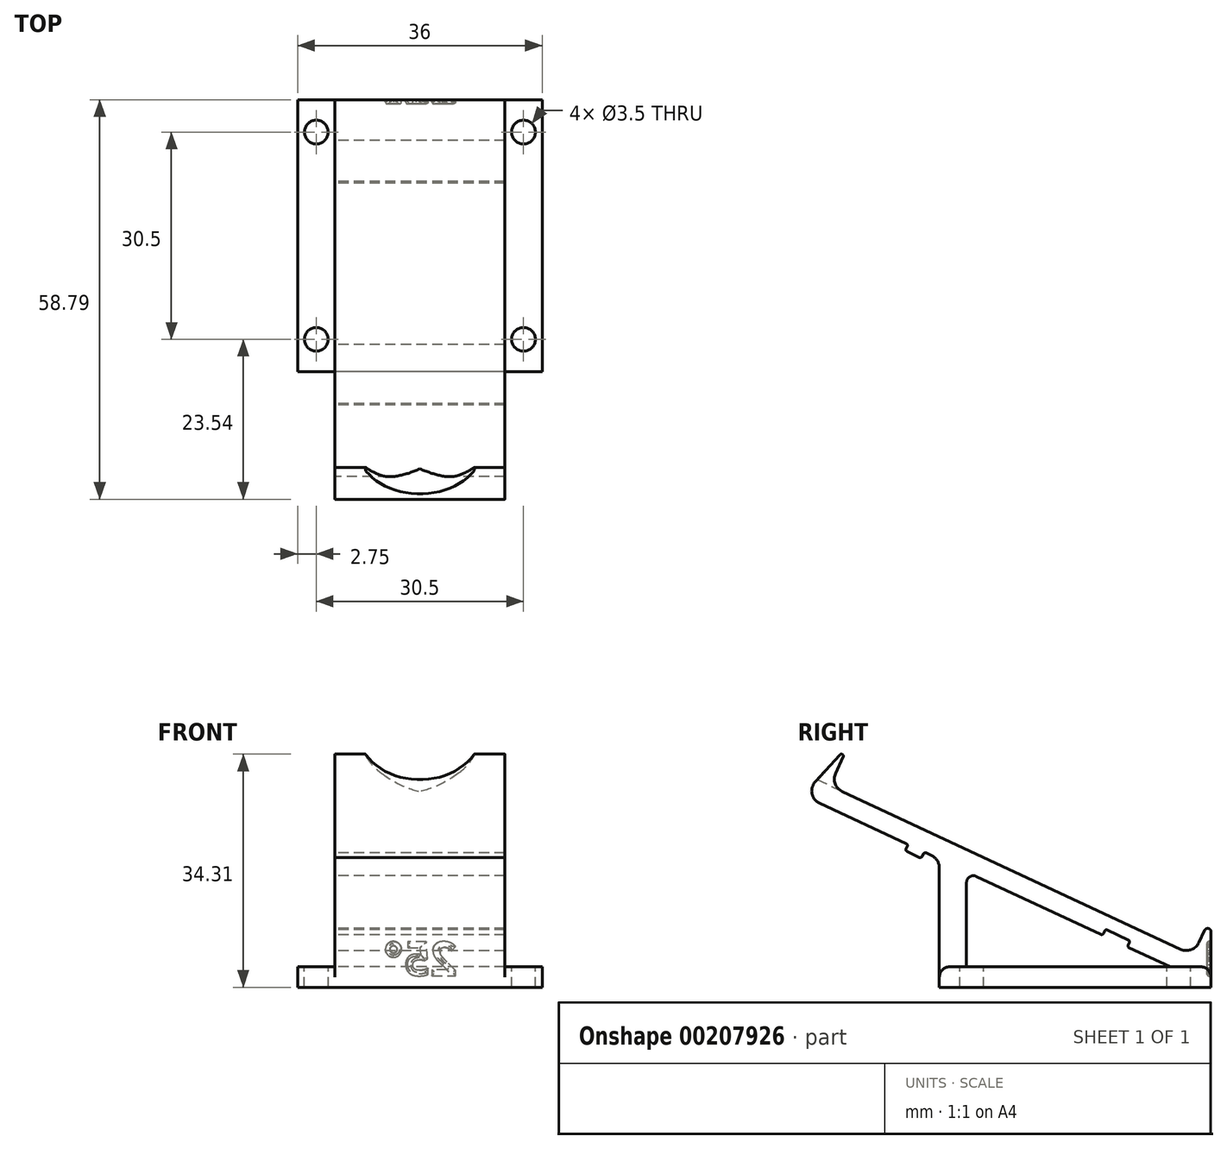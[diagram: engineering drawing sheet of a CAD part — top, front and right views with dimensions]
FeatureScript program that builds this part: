
annotation { "Feature Type Name" : "Feature", "Feature Type Description" : "" }
export const myFeature = defineFeature(function(context is Context, id is Id, definition is map)
    precondition{}
    {
        {
            var Q0;
            Q0=qCreatedBy(makeId("Right.planeOp"),FACE);
            var sketch = newSketch(context, id + "F0", { "sketchPlane" : qUnion([Q0])});
            skLineSegment(sketch, "E0", {"start": v(0, 0) * mm, "end": v(4, 0) * mm});
            skLineSegment(sketch, "E1", {"start": v(24.16, 4.92) * mm, "end": v(24.33, 5.28) * mm});
            skLineSegment(sketch, "E2", {"start": v(24.73, 5.43) * mm, "end": v(27.8, 4) * mm});
            skLineSegment(sketch, "E3", {"start": v(27.95, 3.6) * mm, "end": v(27.78, 3.23) * mm});
            skLineSegment(sketch, "E4", {"start": v(27.93, 2.83) * mm, "end": v(34, 0) * mm});
            skLineSegment(sketch, "E5", {"start": v(40, 0) * mm, "end": v(40, 5.16) * mm});
            skLineSegment(sketch, "E6", {"start": v(39.05, 5.37) * mm, "end": v(38.2, 3.56) * mm});
            skLineSegment(sketch, "E7", {"start": v(35.54, 2.6) * mm, "end": v(-14.3, 25.83) * mm});
            skLineSegment(sketch, "E8", {"start": v(-15.27, 28.5) * mm, "end": v(-14.16, 30.88) * mm});
            skLineSegment(sketch, "E9", {"start": v(-14.65, 31.2) * mm, "end": v(-18.27, 27.24) * mm});
            skLineSegment(sketch, "E10", {"start": v(-17.64, 24.08) * mm, "end": v(-4.86, 18.12) * mm});
            skLineSegment(sketch, "E11", {"start": v(-4.71, 17.72) * mm, "end": v(-4.88, 17.36) * mm});
            skLineSegment(sketch, "E12", {"start": v(-4.74, 16.96) * mm, "end": v(-2.93, 16.12) * mm});
            skLineSegment(sketch, "E13", {"start": v(-2.53, 16.26) * mm, "end": v(-2.36, 16.62) * mm});
            skLineSegment(sketch, "E14", {"start": v(-1.96, 16.77) * mm, "end": v(-1.15, 16.4) * mm});
            skLineSegment(sketch, "E15", {"start": v(0, 14.58) * mm, "end": v(0, 0) * mm});
            skArc(sketch, "E16", {"start": v(23.76, 4.78) * mm, "mid": v(23.99, 4.77) * mm, "end": v(24.16, 4.92) * mm});
            skArc(sketch, "E17", {"start": v(24.33, 5.28) * mm, "mid": v(24.5, 5.44) * mm, "end": v(24.73, 5.43) * mm});
            skArc(sketch, "E18", {"start": v(27.8, 4) * mm, "mid": v(27.96, 3.82) * mm, "end": v(27.95, 3.6) * mm});
            skArc(sketch, "E19", {"start": v(27.78, 3.23) * mm, "mid": v(27.77, 3) * mm, "end": v(27.93, 2.83) * mm});
            skArc(sketch, "E20", {"start": v(35.54, 2.6) * mm, "mid": v(37.07, 2.52) * mm, "end": v(38.2, 3.56) * mm});
            skArc(sketch, "E21", {"start": v(40, 5.16) * mm, "mid": v(39.6, 5.65) * mm, "end": v(39.05, 5.37) * mm});
            skArc(sketch, "E22", {"start": v(-1.15, 16.4) * mm, "mid": v(-0.31, 15.65) * mm, "end": v(0, 14.58) * mm});
            skArc(sketch, "E23", {"start": v(-1.96, 16.77) * mm, "mid": v(-2.19, 16.78) * mm, "end": v(-2.36, 16.62) * mm});
            skArc(sketch, "E24", {"start": v(-2.93, 16.12) * mm, "mid": v(-2.7, 16.1) * mm, "end": v(-2.53, 16.26) * mm});
            skArc(sketch, "E25", {"start": v(-4.74, 16.96) * mm, "mid": v(-4.9, 17.13) * mm, "end": v(-4.88, 17.36) * mm});
            skArc(sketch, "E26", {"start": v(-4.86, 18.12) * mm, "mid": v(-4.7, 17.95) * mm, "end": v(-4.71, 17.72) * mm});
            skArc(sketch, "E27", {"start": v(-17.64, 24.08) * mm, "mid": v(-18.75, 25.5) * mm, "end": v(-18.27, 27.24) * mm});
            skArc(sketch, "E28", {"start": v(-14.65, 31.2) * mm, "mid": v(-14.26, 31.26) * mm, "end": v(-14.16, 30.88) * mm});
            skPoint(sketch, "E29.visualSharp", {"position": v(-16.12, 26.68) * mm});
            skArc(sketch, "E30.filletArc", {"start": v(-15.27, 28.5) * mm, "mid": v(-15.34, 26.96) * mm, "end": v(-14.3, 25.83) * mm});
            skLineSegment(sketch, "E31", {"start": v(34, 0) * mm, "end": v(40, 0) * mm});
            skLineSegment(sketch, "E32", {"start": v(4, 12.42) * mm, "end": v(4, 0) * mm});
            skLineSegment(sketch, "E33", {"start": v(5.42, 13.33) * mm, "end": v(23.76, 4.78) * mm});
            skPoint(sketch, "E34.visualSharp", {"position": v(4, 13.99) * mm});
            skArc(sketch, "E34.filletArc", {"start": v(5.42, 13.33) * mm, "mid": v(4.46, 13.26) * mm, "end": v(4, 12.42) * mm});
            skSolve(sketch);
        }
        {
            var Q0;
            Q0 = qSketchRegion(id + "F0", true);
            extrude(context, id + "F1", {"entities" : qUnion([Q0]), "endBound" : BoundingType.SYMMETRIC, "depth" : 25 * mm});
        }
        {
            var Q0;
            Q0=makeQuery(id+"F1.opExtrude","SWEPT_FACE",FACE,{"disambiguationData":[OSD([sQuery(id+"F0.wireOp",EDGE,"E0")])]});
            var sketch = newSketch(context, id + "F2", { "sketchPlane" : qUnion([Q0])});
            skLineSegment(sketch, "E35.bottom", {"start": v(15.25, -4.75) * mm, "end": v(-15.25, -4.75) * mm, "construction": true});
            skLineSegment(sketch, "E35.top", {"start": v(15.25, -35.25) * mm, "end": v(-15.25, -35.25) * mm, "construction": true});
            skLineSegment(sketch, "E35.left", {"start": v(15.25, -4.75) * mm, "end": v(15.25, -35.25) * mm, "construction": true});
            skLineSegment(sketch, "E35.right", {"start": v(-15.25, -4.75) * mm, "end": v(-15.25, -35.25) * mm, "construction": true});
            skCircle(sketch, "E36", {"center": v(-15.25, -4.75) * mm, "radius": 1.75 * mm});
            skCircle(sketch, "E37", {"center": v(15.25, -4.75) * mm, "radius": 1.75 * mm});
            skCircle(sketch, "E38", {"center": v(15.25, -35.25) * mm, "radius": 1.75 * mm});
            skCircle(sketch, "E39", {"center": v(-15.25, -35.25) * mm, "radius": 1.75 * mm});
            skLineSegment(sketch, "E40", {"start": v(-15.25, -4.75) * mm, "end": v(-15.25, 0) * mm, "construction": true});
            skLineSegment(sketch, "E41", {"start": v(-15.25, -35.25) * mm, "end": v(-15.25, -40) * mm, "construction": true});
            skLineSegment(sketch, "E42.bottom", {"start": v(-18, 0) * mm, "end": v(18, 0) * mm});
            skLineSegment(sketch, "E42.top", {"start": v(-18, -40) * mm, "end": v(18, -40) * mm});
            skLineSegment(sketch, "E42.left", {"start": v(-18, 0) * mm, "end": v(-18, -40) * mm});
            skLineSegment(sketch, "E42.right", {"start": v(18, 0) * mm, "end": v(18, -40) * mm});
            skLineSegment(sketch, "E43", {"start": v(15.25, -4.75) * mm, "end": v(18, -4.75) * mm, "construction": true});
            skLineSegment(sketch, "E44", {"start": v(-15.25, -4.75) * mm, "end": v(-18, -4.75) * mm, "construction": true});
            skPoint(sketch, "E45.endSnap0", {"position": v(0, 0) * mm});
            skLineSegment(sketch, "E46", {"start": v(0, 0) * mm, "end": v(0, -40) * mm, "construction": true});
            skLineSegment(sketch, "E47", {"start": v(-12.42, -20) * mm, "end": v(12.9, -20) * mm, "construction": true});
            skPoint(sketch, "E47.startSnap0", {"position": v(0, -20) * mm});
            skSolve(sketch);
        }
        {
            var Q0;
            Q0 = qSketchRegion(id + "F2", true);
            extrude(context, id + "F3", {"entities" : qUnion([Q0]), "operationType" : NewBodyOperationType.ADD, "depth" : 3 * mm});
        }
        {
            var Q0;
            Q0=makeQuery(id+"F1.opExtrude","SWEPT_FACE",FACE,{"disambiguationData":[OSD([sQuery(id+"F0.wireOp",EDGE,"E8")])]});
            var sketch = newSketch(context, id + "F4", { "sketchPlane" : qUnion([Q0])});
            skCircle(sketch, "E48", {"center": v(0, 26.37) * mm, "radius": 9 * mm});
            skLineSegment(sketch, "E49.0", {"start": v(-12.5, 17.37) * mm, "end": v(12.5, 17.37) * mm, "construction": true});
            skLineSegment(sketch, "E50", {"start": v(0, 17.37) * mm, "end": v(0, 34.14) * mm, "construction": true});
            skSolve(sketch);
        }
        {
            var Q0;
            Q0 = qSketchRegion(id + "F4", true);
            var Q1;
            Q1=makeQuery(id+"F1.opExtrude","SWEPT_FACE",FACE,{"disambiguationData":[OSD([sQuery(id+"F0.wireOp",EDGE,"E9")])]});
            var Q2;
            Q2=makeQuery(id+"F1.opExtrude","SWEPT_FACE",FACE,{"disambiguationData":[OSD([sQuery(id+"F0.wireOp",EDGE,"E7")])]});
            extrude(context, id + "F5", {"entities" : qUnion([Q0]), "operationType" : NewBodyOperationType.REMOVE, "endBound" : BoundingType.UP_TO_SURFACE, "oppositeDirection" : true, "endBoundEntityFace" : qUnion([Q1]), "depth" : 25 * mm, "hasSecondDirection" : true, "secondDirectionOppositeDirection" : false, "secondDirectionBoundEntityFace" : qUnion([Q2]), "secondDirectionDepth" : 2 * mm});
        }
        {
            var Q0;
            {var subQ0=sQuery(id+"F2.wireOp",EDGE,"E42.bottom");var subQ1=sQuery(id+"F2.wireOp",EDGE,"E42.right");Q0=makeQuery(id+"F3.boolean.opBoolean","SPLIT",EDGE,{"disambiguationData":[TD([makeQuery(id+"F3.opExtrude","SWEPT_FACE",FACE,{"disambiguationData":[OSD([subQ1])]})])],"derivedFrom":makeQuery(id+"F3.opExtrude","CAP_EDGE",EDGE,{"disambiguationData":[OSD([subQ0])],"isStart":true})});}
            var Q1;
            {var subQ0=sQuery(id+"F2.wireOp",EDGE,"E42.top");var subQ1=sQuery(id+"F2.wireOp",EDGE,"E42.right");Q1=makeQuery(id+"F3.boolean.opBoolean","SPLIT",EDGE,{"disambiguationData":[TD([makeQuery(id+"F3.opExtrude","SWEPT_FACE",FACE,{"disambiguationData":[OSD([subQ1])]})])],"derivedFrom":makeQuery(id+"F3.opExtrude","CAP_EDGE",EDGE,{"disambiguationData":[OSD([subQ0])],"isStart":true})});}
            var Q2;
            {var subQ0=sQuery(id+"F2.wireOp",EDGE,"E42.top");var subQ1=sQuery(id+"F2.wireOp",EDGE,"E42.left");Q2=makeQuery(id+"F3.boolean.opBoolean","SPLIT",EDGE,{"disambiguationData":[TD([makeQuery(id+"F3.opExtrude","SWEPT_FACE",FACE,{"disambiguationData":[OSD([subQ1])]})])],"derivedFrom":makeQuery(id+"F3.opExtrude","CAP_EDGE",EDGE,{"disambiguationData":[OSD([subQ0])],"isStart":true})});}
            var Q3;
            {var subQ0=sQuery(id+"F2.wireOp",EDGE,"E42.bottom");var subQ2=sQuery(id+"F2.wireOp",EDGE,"E42.left");Q3=makeQuery(id+"F3.boolean.opBoolean","SPLIT",EDGE,{"disambiguationData":[TD([makeQuery(id+"F3.opExtrude","SWEPT_FACE",FACE,{"disambiguationData":[OSD([subQ2])]})])],"derivedFrom":makeQuery(id+"F3.opExtrude","CAP_EDGE",EDGE,{"disambiguationData":[OSD([subQ0])],"isStart":true})});}
            var Q4;
            Q4=makeQuery(id+"F1.opExtrude","SWEPT_EDGE",EDGE,{"disambiguationData":[OSD([sQuery(id+"F0.wireOp",EDGE,"E0"),sQuery(id+"F0.wireOp",EDGE,"E32")])]});
            fillet(context, id + "F6", {"entities" : qUnion([Q0, Q1, Q2, Q3, Q4]), "radius" : 1.5 * mm, "tangentPropagation" : true, "allowEdgeOverflow" : false});
        }
        {
            var Q0;
            Q0=makeQuery(id+"F3.boolean.opBoolean","MERGE",FACE,{"derivedFrom":[makeQuery(id+"F1.opExtrude","SWEPT_FACE",FACE,{"disambiguationData":[OSD([sQuery(id+"F0.wireOp",EDGE,"E5")])]}),makeQuery(id+"F3.opExtrude","SWEPT_FACE",FACE,{"disambiguationData":[OSD([sQuery(id+"F2.wireOp",EDGE,"a0c96e45-3273-4dbd-95e5-2c47b5aee7d6.top")])]})]});
            var sketch = newSketch(context, id + "F7", { "sketchPlane" : qUnion([Q0])});
            skText(sketch, "E51", { "text": "25°", "fontName": "OpenSans-Bold.ttf"});
            skPoint(sketch, "E52.startSnap0", {"position": v(0, 1.08) * mm});
            skPoint(sketch, "E52.endSnap0", {"position": v(0, 1.08) * mm});
            skLineSegment(sketch, "E53.0", {"start": v(12.5, -1.5) * mm, "end": v(12.5, 5.16) * mm, "construction": true});
            skLineSegment(sketch, "E54.0", {"start": v(-12.5, 5.16) * mm, "end": v(12.5, 5.16) * mm, "construction": true});
            skLineSegment(sketch, "E55.0", {"start": v(-12.5, -1.5) * mm, "end": v(-12.5, 5.16) * mm, "construction": true});
            skLineSegment(sketch, "E56", {"start": v(5.52, 3.58) * mm, "end": v(5.52, 5.16) * mm, "construction": true});
            skLineSegment(sketch, "E57", {"start": v(5.52, -1.42) * mm, "end": v(5.52, -3) * mm, "construction": true});
            skLineSegment(sketch, "E58.0", {"start": v(18, -3) * mm, "end": v(-18, -3) * mm, "construction": true});
            skLineSegment(sketch, "E59", {"start": v(-5.52, 3.58) * mm, "end": v(-12.5, 3.58) * mm, "construction": true});
            skLineSegment(sketch, "E60", {"start": v(5.52, 3.58) * mm, "end": v(12.5, 3.58) * mm, "construction": true});
            const initialGuessF7  = {"E51": [-0.00552, -0.00128, 1, 0, 0.005]};
            skSetInitialGuess(sketch, initialGuessF7);
            skSolve(sketch);
        }
        {
            var Q0;
            Q0 = qSketchRegion(id + "F7", true);
            extrude(context, id + "F8", {"entities" : qUnion([Q0]), "operationType" : NewBodyOperationType.REMOVE, "oppositeDirection" : true, "depth" : .6 * mm});
        }
        {
            var Q0;
            Q0=makeQuery(id+"F8.boolean.opBoolean","COPY",FACE,{"derivedFrom":makeQuery(id+"F8.opExtrude","CAP_FACE",FACE,{"disambiguationData":[OSD([sQuery(id+"F7.wireOp",EDGE,"E51.sketch_text.stroke-22"),sQuery(id+"F7.wireOp",EDGE,"E51.sketch_text.stroke-23"),sQuery(id+"F7.wireOp",EDGE,"E51.sketch_text.stroke-24"),sQuery(id+"F7.wireOp",EDGE,"E51.sketch_text.stroke-25"),sQuery(id+"F7.wireOp",EDGE,"E51.sketch_text.stroke-26"),sQuery(id+"F7.wireOp",EDGE,"E51.sketch_text.stroke-27"),sQuery(id+"F7.wireOp",EDGE,"E51.sketch_text.stroke-28"),sQuery(id+"F7.wireOp",EDGE,"E51.sketch_text.stroke-29"),sQuery(id+"F7.wireOp",EDGE,"E51.sketch_text.stroke-30"),sQuery(id+"F7.wireOp",EDGE,"E51.sketch_text.stroke-31"),sQuery(id+"F7.wireOp",EDGE,"E51.sketch_text.stroke-32"),sQuery(id+"F7.wireOp",EDGE,"E51.sketch_text.stroke-33"),sQuery(id+"F7.wireOp",EDGE,"E51.sketch_text.stroke-34"),sQuery(id+"F7.wireOp",EDGE,"E51.sketch_text.stroke-35"),sQuery(id+"F7.wireOp",EDGE,"E51.sketch_text.stroke-36"),sQuery(id+"F7.wireOp",EDGE,"E51.sketch_text.stroke-37"),sQuery(id+"F7.wireOp",EDGE,"E51.sketch_text.stroke-38"),sQuery(id+"F7.wireOp",EDGE,"E51.sketch_text.stroke-39"),sQuery(id+"F7.wireOp",EDGE,"E51.sketch_text.stroke-40"),sQuery(id+"F7.wireOp",EDGE,"E51.sketch_text.stroke-41"),sQuery(id+"F7.wireOp",EDGE,"E51.sketch_text.stroke-42"),sQuery(id+"F7.wireOp",EDGE,"E51.sketch_text.stroke-43")])],"isStart":false})});
            var Q1;
            Q1=makeQuery(id+"F8.boolean.opBoolean","COPY",FACE,{"derivedFrom":makeQuery(id+"F8.opExtrude","CAP_FACE",FACE,{"disambiguationData":[OSD([sQuery(id+"F7.wireOp",EDGE,"E51.sketch_text.stroke-0"),sQuery(id+"F7.wireOp",EDGE,"E51.sketch_text.stroke-1"),sQuery(id+"F7.wireOp",EDGE,"E51.sketch_text.stroke-2"),sQuery(id+"F7.wireOp",EDGE,"E51.sketch_text.stroke-3"),sQuery(id+"F7.wireOp",EDGE,"E51.sketch_text.stroke-4"),sQuery(id+"F7.wireOp",EDGE,"E51.sketch_text.stroke-5"),sQuery(id+"F7.wireOp",EDGE,"E51.sketch_text.stroke-6"),sQuery(id+"F7.wireOp",EDGE,"E51.sketch_text.stroke-7"),sQuery(id+"F7.wireOp",EDGE,"E51.sketch_text.stroke-8"),sQuery(id+"F7.wireOp",EDGE,"E51.sketch_text.stroke-9"),sQuery(id+"F7.wireOp",EDGE,"E51.sketch_text.stroke-10"),sQuery(id+"F7.wireOp",EDGE,"E51.sketch_text.stroke-11"),sQuery(id+"F7.wireOp",EDGE,"E51.sketch_text.stroke-12"),sQuery(id+"F7.wireOp",EDGE,"E51.sketch_text.stroke-13"),sQuery(id+"F7.wireOp",EDGE,"E51.sketch_text.stroke-14"),sQuery(id+"F7.wireOp",EDGE,"E51.sketch_text.stroke-15"),sQuery(id+"F7.wireOp",EDGE,"E51.sketch_text.stroke-16"),sQuery(id+"F7.wireOp",EDGE,"E51.sketch_text.stroke-17"),sQuery(id+"F7.wireOp",EDGE,"E51.sketch_text.stroke-18"),sQuery(id+"F7.wireOp",EDGE,"E51.sketch_text.stroke-19"),sQuery(id+"F7.wireOp",EDGE,"E51.sketch_text.stroke-20"),sQuery(id+"F7.wireOp",EDGE,"E51.sketch_text.stroke-21")])],"isStart":false})});
            var Q2;
            Q2=makeQuery(id+"F8.boolean.opBoolean","COPY",FACE,{"derivedFrom":makeQuery(id+"F8.opExtrude","CAP_FACE",FACE,{"disambiguationData":[OSD([sQuery(id+"F7.wireOp",EDGE,"E51.sketch_text.stroke-44"),sQuery(id+"F7.wireOp",EDGE,"E51.sketch_text.stroke-45"),sQuery(id+"F7.wireOp",EDGE,"E51.sketch_text.stroke-46"),sQuery(id+"F7.wireOp",EDGE,"E51.sketch_text.stroke-47"),sQuery(id+"F7.wireOp",EDGE,"E51.sketch_text.stroke-48"),sQuery(id+"F7.wireOp",EDGE,"E51.sketch_text.stroke-49"),sQuery(id+"F7.wireOp",EDGE,"E51.sketch_text.stroke-50"),sQuery(id+"F7.wireOp",EDGE,"E51.sketch_text.stroke-51"),sQuery(id+"F7.wireOp",EDGE,"E51.sketch_text.stroke-52"),sQuery(id+"F7.wireOp",EDGE,"E51.sketch_text.stroke-53"),sQuery(id+"F7.wireOp",EDGE,"E51.sketch_text.stroke-54"),sQuery(id+"F7.wireOp",EDGE,"E51.sketch_text.stroke-55"),sQuery(id+"F7.wireOp",EDGE,"E51.sketch_text.stroke-56"),sQuery(id+"F7.wireOp",EDGE,"E51.sketch_text.stroke-57"),sQuery(id+"F7.wireOp",EDGE,"E51.sketch_text.stroke-58"),sQuery(id+"F7.wireOp",EDGE,"E51.sketch_text.stroke-59"),sQuery(id+"F7.wireOp",EDGE,"E51.sketch_text.stroke-60"),sQuery(id+"F7.wireOp",EDGE,"E51.sketch_text.stroke-61"),sQuery(id+"F7.wireOp",EDGE,"E51.sketch_text.stroke-62")])],"isStart":false})});
            var Q3;
            Q3=makeQuery(id+"F8.boolean.opBoolean","COPY",FACE,{"derivedFrom":makeQuery(id+"F8.opExtrude","CAP_FACE",FACE,{"disambiguationData":[OSD([sQuery(id+"F7.wireOp",EDGE,"E51.sketch_text.stroke-10"),sQuery(id+"F7.wireOp",EDGE,"E51.sketch_text.stroke-11"),sQuery(id+"F7.wireOp",EDGE,"E51.sketch_text.stroke-12"),sQuery(id+"F7.wireOp",EDGE,"E51.sketch_text.stroke-13"),sQuery(id+"F7.wireOp",EDGE,"E51.sketch_text.stroke-14"),sQuery(id+"F7.wireOp",EDGE,"E51.sketch_text.stroke-15"),sQuery(id+"F7.wireOp",EDGE,"E51.sketch_text.stroke-16"),sQuery(id+"F7.wireOp",EDGE,"E51.sketch_text.stroke-17"),sQuery(id+"F7.wireOp",EDGE,"E51.sketch_text.stroke-18"),sQuery(id+"F7.wireOp",EDGE,"E51.sketch_text.stroke-19"),sQuery(id+"F7.wireOp",EDGE,"E51.sketch_text.stroke-20"),sQuery(id+"F7.wireOp",EDGE,"E51.sketch_text.stroke-21"),sQuery(id+"F7.wireOp",EDGE,"E51.sketch_text.stroke-22"),sQuery(id+"F7.wireOp",EDGE,"E51.sketch_text.stroke-23"),sQuery(id+"F7.wireOp",EDGE,"E51.sketch_text.stroke-24"),sQuery(id+"F7.wireOp",EDGE,"E51.sketch_text.stroke-25")])],"isStart":false})});
            var Q4;
            Q4=makeQuery(id+"F8.boolean.opBoolean","COPY",FACE,{"derivedFrom":makeQuery(id+"F8.opExtrude","CAP_FACE",FACE,{"disambiguationData":[OSD([sQuery(id+"F7.wireOp",EDGE,"E51.sketch_text.stroke-0"),sQuery(id+"F7.wireOp",EDGE,"E51.sketch_text.stroke-1"),sQuery(id+"F7.wireOp",EDGE,"E51.sketch_text.stroke-2"),sQuery(id+"F7.wireOp",EDGE,"E51.sketch_text.stroke-3"),sQuery(id+"F7.wireOp",EDGE,"E51.sketch_text.stroke-4"),sQuery(id+"F7.wireOp",EDGE,"E51.sketch_text.stroke-5"),sQuery(id+"F7.wireOp",EDGE,"E51.sketch_text.stroke-6")])],"isStart":false})});
            fillet(context, id + "F9", {"entities" : qUnion([Q0, Q1, Q2, Q3, Q4]), "radius" : .3 * mm, "tangentPropagation" : true, "allowEdgeOverflow" : false});
        }
    });
